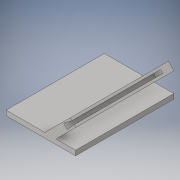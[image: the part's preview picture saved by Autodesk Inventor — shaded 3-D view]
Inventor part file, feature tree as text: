
AUTODESK INVENTOR PART (.ipt)
format: ipt  version: 2016 (Build 200138000, 138)  size: 114,176 bytes
history: native  units: in
note: dims shown in document units (in); Inventor stores cm internally (conversion verified against a paired STEP export)
features: extrude x2, sketch x1
ambient origin geometry x8: Origin, YZ Plane, XZ Plane, XY Plane, X Axis, Y Axis, Z Axis, Center Point
bodies: Solid1 (feature_tree)
feature tree (3):
  extrude  "Extrusion1"  Depth=0.25in
  extrude  "Extrusion5"  TaperAngle=90.0deg  [1 undecoded]
  sketch  "Sketch5"  dims[d4=1.0in d7=0.25in d8=90.0deg d9=135.0deg d10=0.4in d11=135.0deg d12=5.0in d13=0.0in d28=0.17in d29=0.27in d30=0.52in d31=4.52in d32=0.0in]
note: 1 required parameter value undecoded (feature->parameter linkage not recoverable at this tier; creation-order binding heuristic only, values carry confidence <= 0.55)
